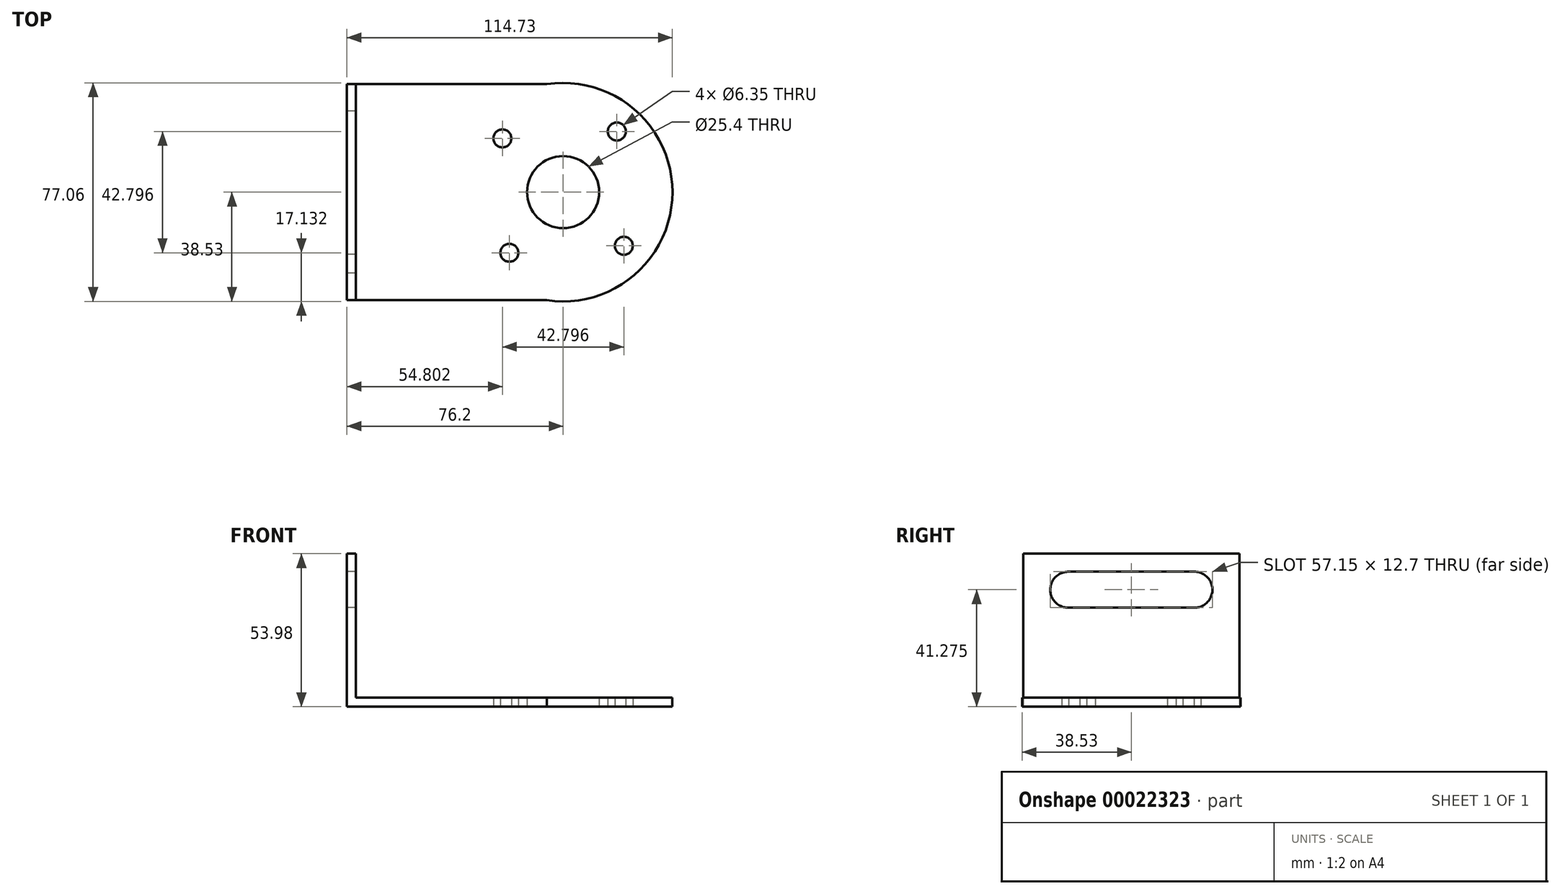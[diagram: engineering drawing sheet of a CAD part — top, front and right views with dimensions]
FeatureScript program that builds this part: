
annotation { "Feature Type Name" : "Feature", "Feature Type Description" : "" }
export const myFeature = defineFeature(function(context is Context, id is Id, definition is map)
    precondition{}
    {
        {
            var Q0;
            Q0=qCreatedBy(makeId("Top.planeOp"),FACE);
            var sketch = newSketch(context, id + "F0", { "sketchPlane" : qUnion([Q0])});
            skLineSegment(sketch, "E0.bottom", {"start": v(0, 0) * mm, "end": v(76.2, 0) * mm});
            skLineSegment(sketch, "E0.top", {"start": v(0, 76.2) * mm, "end": v(76.2, 76.2) * mm});
            skLineSegment(sketch, "E0.left", {"start": v(0, 0) * mm, "end": v(0, 76.2) * mm});
            skArc(sketch, "E1", {"start": v(70.47, 0) * mm, "mid": v(114.73, 38.1) * mm, "end": v(70.47, 76.2) * mm});
            skCircle(sketch, "E2", {"center": v(76.2, 38.1) * mm, "radius": 12.7 * mm});
            skCircle(sketch, "E3", {"center": v(54.8, 57.04) * mm, "radius": 3.18 * mm});
            skLineSegment(sketch, "E4", {"start": v(100.34, 22.82) * mm, "end": v(100.34, 22.82) * mm});
            skLineSegment(sketch, "E5.trimOffspring", {"start": v(76.2, 38.1) * mm, "end": v(76.2, 38.1) * mm});
            skCircle(sketch, "E6.1.0", {"center": v(57.26, 16.7) * mm, "radius": 3.18 * mm});
            skCircle(sketch, "E6.2.0", {"center": v(97.6, 19.16) * mm, "radius": 3.18 * mm});
            skCircle(sketch, "E7.1.3.0", {"center": v(95.14, 59.5) * mm, "radius": 3.18 * mm});
            skPoint(sketch, "E8.trimOffspring.end.orphan", {"position": v(124.19, 38.1) * mm});
            skSolve(sketch);
        }
        {
            var Q0;
            Q0=qCreatedBy(makeId("Right.planeOp"),FACE);
            var sketch = newSketch(context, id + "F1", { "sketchPlane" : qUnion([Q0])});
            skLineSegment(sketch, "E9.bottom", {"start": v(0, 53.97) * mm, "end": v(76.2, 53.97) * mm});
            skLineSegment(sketch, "E9.top", {"start": v(0, 0) * mm, "end": v(76.2, 0) * mm});
            skLineSegment(sketch, "E9.left", {"start": v(0, 53.97) * mm, "end": v(0, 0) * mm});
            skLineSegment(sketch, "E9.right", {"start": v(76.2, 53.97) * mm, "end": v(76.2, 0) * mm});
            skLineSegment(sketch, "E10", {"start": v(0, 41.27) * mm, "end": v(76.2, 41.28) * mm, "construction": true});
            skArc(sketch, "E11", {"start": v(60.33, 34.93) * mm, "mid": v(66.67, 41.28) * mm, "end": v(60.32, 47.62) * mm});
            skArc(sketch, "E12", {"start": v(16.11, 47.62) * mm, "mid": v(9.53, 41.4) * mm, "end": v(15.88, 34.92) * mm});
            skLineSegment(sketch, "E13", {"start": v(15.88, 34.92) * mm, "end": v(60.33, 34.92) * mm});
            skLineSegment(sketch, "E14", {"start": v(16.11, 47.62) * mm, "end": v(60.32, 47.62) * mm});
            skSolve(sketch);
        }
        {
            var Q0;
            Q0 = qSketchRegion(id + "F1", true);
            extrude(context, id + "F2", {"entities" : qUnion([Q0]), "depth" : 3.17 * mm});
        }
        {
            var Q0;
            Q0 = qSketchRegion(id + "F0", true);
            extrude(context, id + "F3", {"entities" : qUnion([Q0]), "operationType" : NewBodyOperationType.ADD, "depth" : 3.17 * mm});
        }
    });
